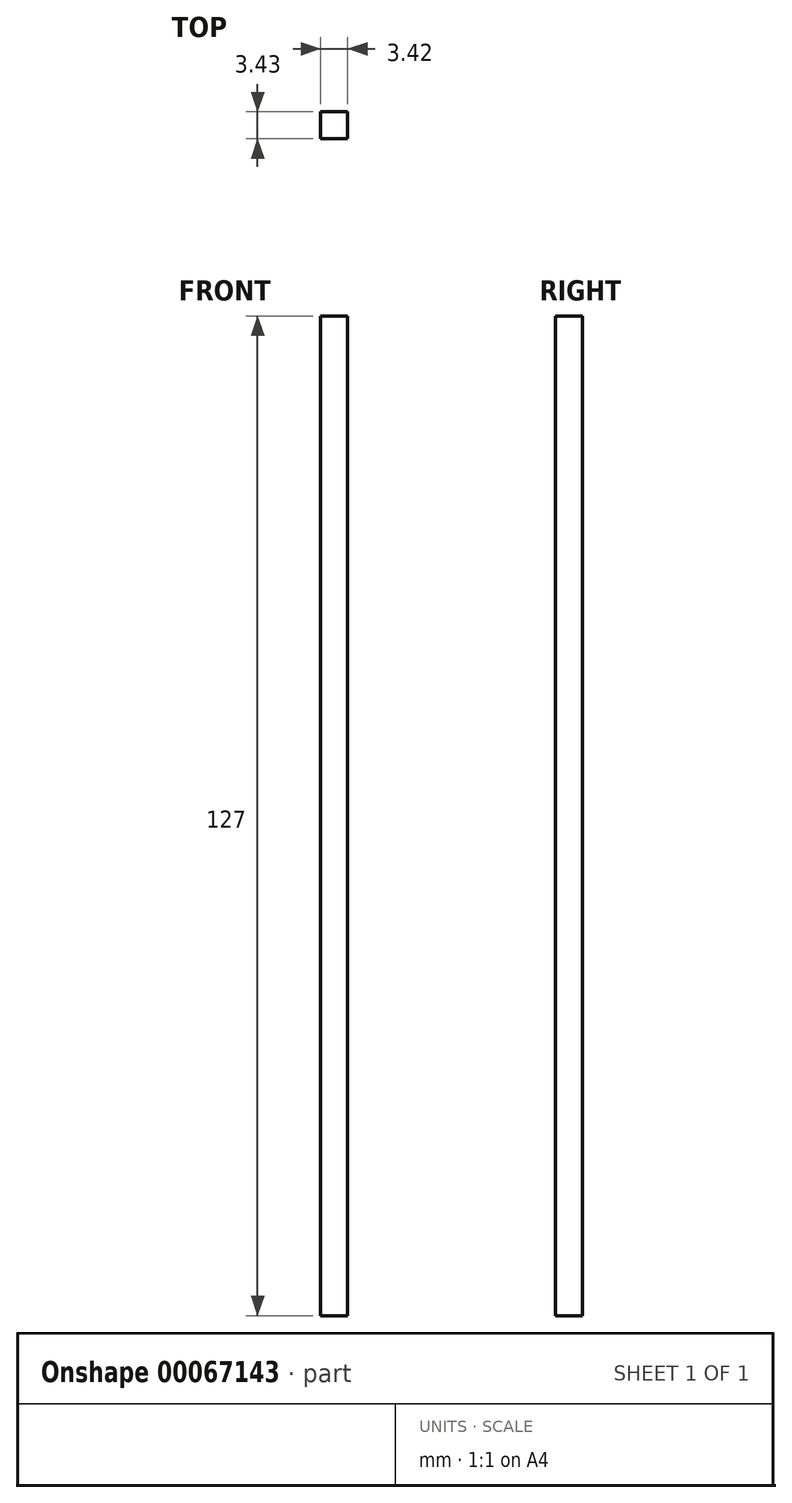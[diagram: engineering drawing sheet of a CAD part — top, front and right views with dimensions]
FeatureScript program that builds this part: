
annotation { "Feature Type Name" : "Feature", "Feature Type Description" : "" }
export const myFeature = defineFeature(function(context is Context, id is Id, definition is map)
    precondition{}
    {
        {
            var Q0;
            Q0=qCreatedBy(makeId("Top.planeOp"),FACE);
            var sketch = newSketch(context, id + "F0", { "sketchPlane" : qUnion([Q0])});
            skLineSegment(sketch, "E0.bottom", {"start": v(-49.6, 20.8) * mm, "end": v(-46.18, 20.8) * mm});
            skLineSegment(sketch, "E0.top", {"start": v(-49.6, 17.37) * mm, "end": v(-46.18, 17.37) * mm});
            skLineSegment(sketch, "E0.left", {"start": v(-49.6, 20.8) * mm, "end": v(-49.6, 17.37) * mm});
            skLineSegment(sketch, "E0.right", {"start": v(-46.18, 20.8) * mm, "end": v(-46.18, 17.37) * mm});
            skSolve(sketch);
        }
        {
            var Q0;
            Q0=makeQuery(id+"F0.imprint","IMPRINT",FACE,{"disambiguationData":[TD([[makeQuery(id+"F0.imprint","IMPRINT",EDGE,{"derivedFrom":sQuery(id+"F0.wireOp",EDGE,"E0.bottom")}),-1.0]])]});
            extrude(context, id + "F1", {"entities" : qUnion([Q0]), "depth" : 127 * mm});
        }
    });
